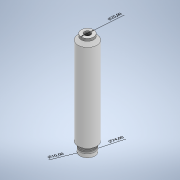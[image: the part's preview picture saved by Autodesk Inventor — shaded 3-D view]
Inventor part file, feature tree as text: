
AUTODESK INVENTOR PART (.ipt)
format: ipt  version: 2021 (Build 250183000, 183)  size: 145,920 bytes
history: native  units: mm
features: other x7, extrude x4, sketch x4, chamfer x2
ambient origin geometry x8: Origin, YZ Plane, XZ Plane, XY Plane, X Axis, Y Axis, Z Axis, Center Point
bodies: Solide1 (feature_tree)
feature tree (17):
  other  "Annotations"
  extrude  "Extrusion1"  Depth=30.0mm
  extrude  "Extrusion2"  Depth=150.0mm TaperAngle=0.0deg
  other  "Filetage2"
  chamfer  "Chanfrein1"  Distance=20.0mm
  chamfer  "Chanfrein2"  Distance=154.0mm
  extrude  "Extrusion4"  Depth=4.0mm TaperAngle=0.0deg
  extrude  "Extrusion3"  Depth=154.0mm TaperAngle=0.0deg
  other  "Filetage5"
  sketch  "Esquisse1"
  sketch  "Esquisse2"
  sketch  "Esquisse3"
  sketch  "Esquisse5"
  other  "Cote de diamètre 1"
  other  "Cote de diamètre 2"
  other  "Cote de diamètre 3"
  other  "Cote de diamètre 4"
